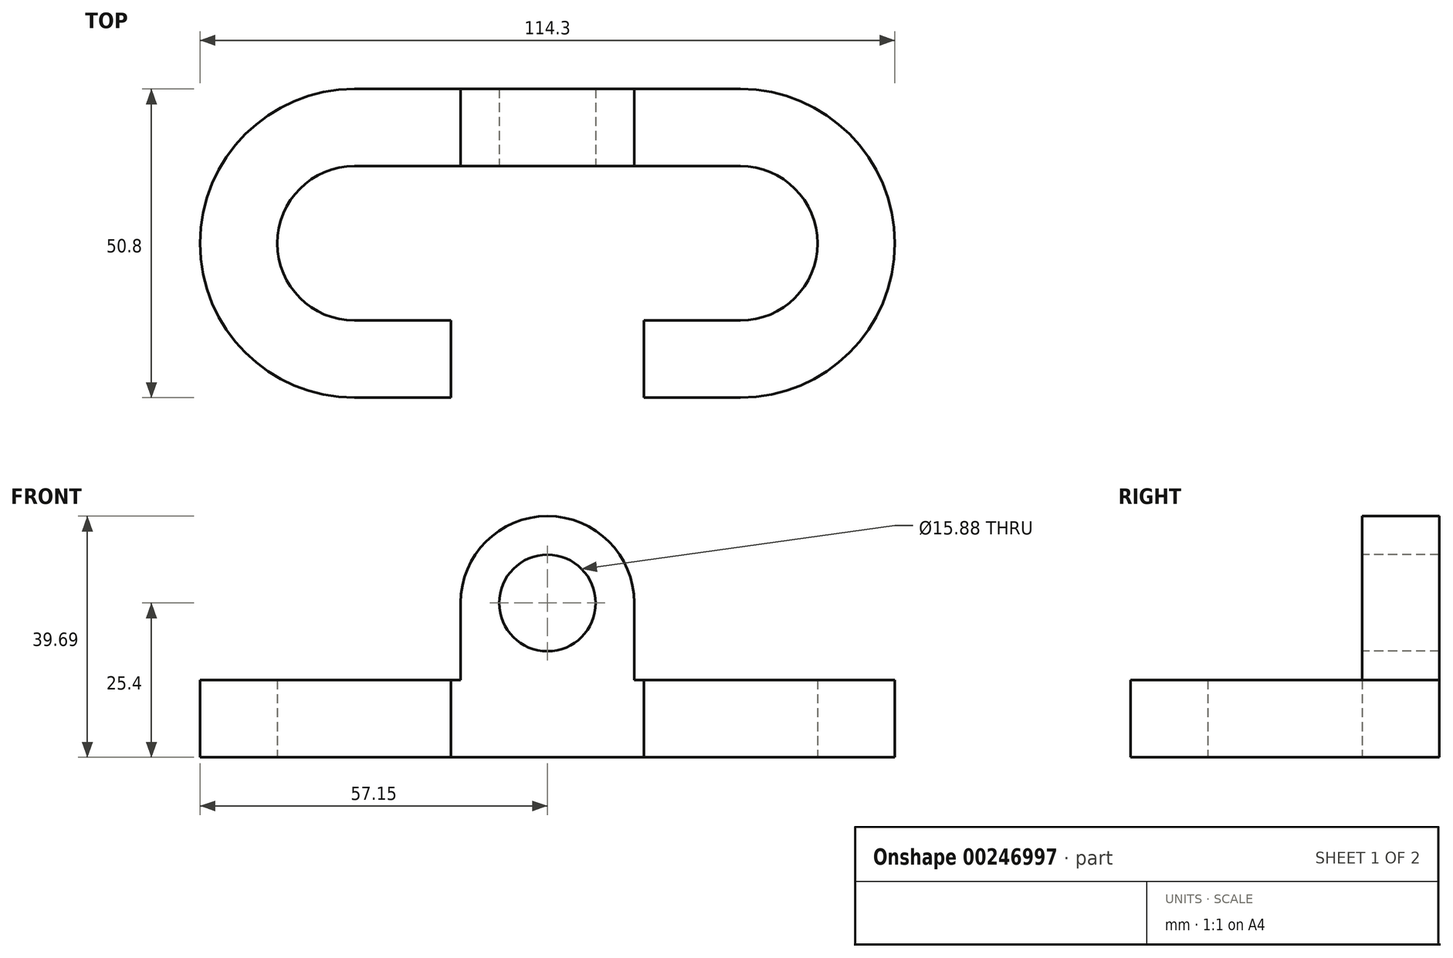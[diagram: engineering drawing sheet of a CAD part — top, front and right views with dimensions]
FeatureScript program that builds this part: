
annotation { "Feature Type Name" : "Feature", "Feature Type Description" : "" }
export const myFeature = defineFeature(function(context is Context, id is Id, definition is map)
    precondition{}
    {
        {
            var Q0;
            Q0=qCreatedBy(makeId("Top.planeOp"),FACE);
            var sketch = newSketch(context, id + "F0", { "sketchPlane" : qUnion([Q0])});
            skArc(sketch, "E0", {"start": v(31.75, -12.7) * mm, "mid": v(44.45, 0) * mm, "end": v(31.75, 12.7) * mm});
            skArc(sketch, "E1", {"start": v(31.75, -25.4) * mm, "mid": v(57.15, 0) * mm, "end": v(31.75, 25.4) * mm});
            skLineSegment(sketch, "E2", {"start": v(31.75, 12.7) * mm, "end": v(0, 12.7) * mm});
            skLineSegment(sketch, "E3", {"start": v(31.75, 25.4) * mm, "end": v(0, 25.4) * mm});
            skLineSegment(sketch, "E4", {"start": v(31.75, -12.7) * mm, "end": v(15.88, -12.7) * mm});
            skLineSegment(sketch, "E5", {"start": v(31.75, -25.4) * mm, "end": v(15.88, -25.4) * mm});
            skLineSegment(sketch, "E6", {"start": v(15.88, -25.4) * mm, "end": v(15.88, -12.7) * mm});
            skLineSegment(sketch, "E7.MirrorCS", {"start": v(-31.75, 25.4) * mm, "end": v(0, 25.4) * mm});
            skArc(sketch, "E8.MirrorCS", {"start": v(-31.75, -25.4) * mm, "mid": v(-57.15, 0) * mm, "end": v(-31.75, 25.4) * mm});
            skLineSegment(sketch, "E9.MirrorCS", {"start": v(-31.75, 12.7) * mm, "end": v(0, 12.7) * mm});
            skArc(sketch, "E10.MirrorCS", {"start": v(-31.75, -12.7) * mm, "mid": v(-44.45, 0) * mm, "end": v(-31.75, 12.7) * mm});
            skLineSegment(sketch, "E11.MirrorCS", {"start": v(-31.75, -12.7) * mm, "end": v(-15.88, -12.7) * mm});
            skLineSegment(sketch, "E12.MirrorCS", {"start": v(-15.88, -25.4) * mm, "end": v(-15.88, -12.7) * mm});
            skLineSegment(sketch, "E13.MirrorCS", {"start": v(-31.75, -25.4) * mm, "end": v(-15.88, -25.4) * mm});
            skSolve(sketch);
        }
        {
            var Q0;
            Q0 = qSketchRegion(id + "F0", true);
            extrude(context, id + "F1", {"entities" : qUnion([Q0]), "depth" : 12.7 * mm});
        }
        {
            var Q0;
            Q0=makeQuery(id+"F1.opExtrude","SWEPT_FACE",FACE,{"disambiguationData":[OSD([sQuery(id+"F0.wireOp",EDGE,"E2"),sQuery(id+"F0.wireOp",EDGE,"E9.MirrorCS")])]});
            var sketch = newSketch(context, id + "F2", { "sketchPlane" : qUnion([Q0])});
            skCircle(sketch, "E14", {"center": v(0, 25.4) * mm, "radius": 7.94 * mm});
            skPoint(sketch, "E14.centerSnap0", {"position": v(0, 12.7) * mm});
            skArc(sketch, "E15", {"start": v(14.29, 25.4) * mm, "mid": v(0, 39.69) * mm, "end": v(-14.29, 25.4) * mm});
            skLineSegment(sketch, "E16", {"start": v(14.29, 25.4) * mm, "end": v(14.29, 12.7) * mm});
            skLineSegment(sketch, "E17", {"start": v(-14.29, 25.4) * mm, "end": v(-14.29, 12.7) * mm});
            skLineSegment(sketch, "E18", {"start": v(-14.29, 12.7) * mm, "end": v(14.29, 12.7) * mm});
            skSolve(sketch);
        }
        {
            var Q0;
            Q0 = qSketchRegion(id + "F2", true);
            extrude(context, id + "F3", {"entities" : qUnion([Q0]), "operationType" : NewBodyOperationType.ADD, "oppositeDirection" : true, "depth" : 12.7 * mm});
        }
    });
